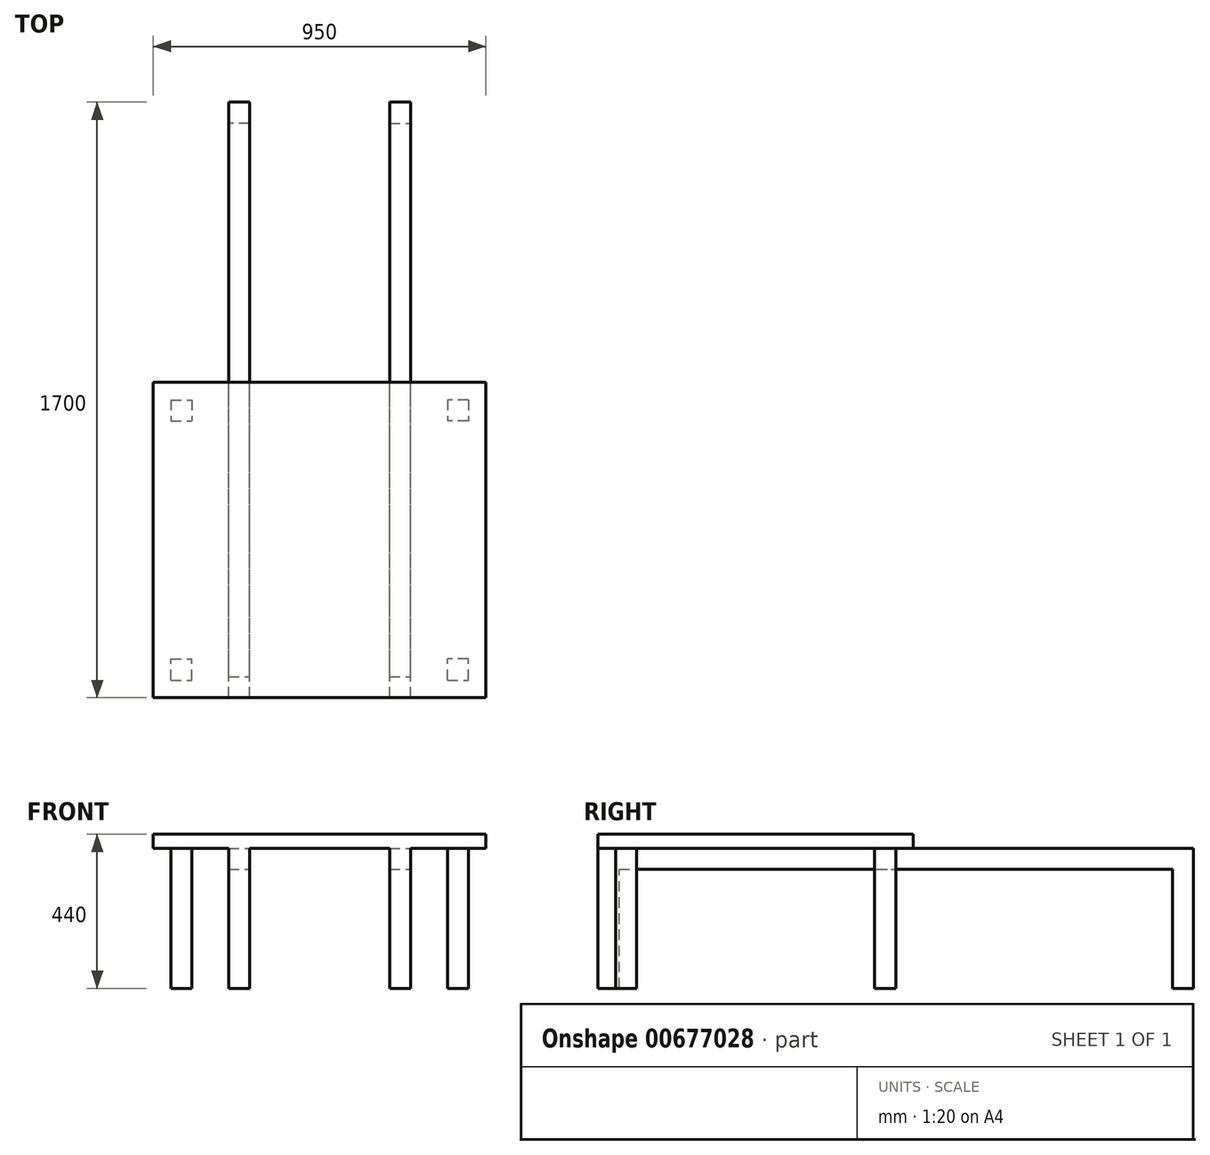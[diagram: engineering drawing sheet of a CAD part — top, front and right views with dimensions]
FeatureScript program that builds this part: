
annotation { "Feature Type Name" : "Feature", "Feature Type Description" : "" }
export const myFeature = defineFeature(function(context is Context, id is Id, definition is map)
    precondition{}
    {
        {
            var Q0;
            Q0=qCreatedBy(makeId("Top.planeOp"),FACE);
            var sketch = newSketch(context, id + "F0", { "sketchPlane" : qUnion([Q0])});
            skLineSegment(sketch, "E0", {"start": v(0, 1100) * mm, "end": v(0, 0) * mm, "construction": true});
            skLineSegment(sketch, "E1", {"start": v(-735, 500) * mm, "end": v(-735, 0) * mm, "construction": true});
            skLineSegment(sketch, "E2", {"start": v(-735, 0) * mm, "end": v(-485, 0) * mm, "construction": true});
            skLineSegment(sketch, "E3", {"start": v(-485, 0) * mm, "end": v(-735, 500) * mm, "construction": true});
            skLineSegment(sketch, "E4", {"start": v(735, 500) * mm, "end": v(485, 0) * mm, "construction": true});
            skLineSegment(sketch, "E5", {"start": v(-485, 496.22) * mm, "end": v(-485, 0) * mm});
            skLineSegment(sketch, "E6", {"start": v(485, 496.22) * mm, "end": v(485, 0) * mm});
            skLineSegment(sketch, "E7", {"start": v(-735, 500) * mm, "end": v(-735, 0) * mm});
            skLineSegment(sketch, "E8", {"start": v(-485, 0) * mm, "end": v(-485, 500) * mm});
            skLineSegment(sketch, "E9", {"start": v(-485, 500) * mm, "end": v(-735, 500) * mm});
            skLineSegment(sketch, "E10.MirrorCS", {"start": v(485, 500) * mm, "end": v(735, 500) * mm});
            skLineSegment(sketch, "E11.MirrorCS", {"start": v(485, 0) * mm, "end": v(485, 500) * mm});
            skLineSegment(sketch, "E12.MirrorCS", {"start": v(735, 0) * mm, "end": v(485, 0) * mm, "construction": true});
            skLineSegment(sketch, "E13.MirrorCS", {"start": v(735, 500) * mm, "end": v(735, 0) * mm, "construction": true});
            skLineSegment(sketch, "E14.top", {"start": v(-625, 1100) * mm, "end": v(625, 1100) * mm, "construction": true});
            skLineSegment(sketch, "E15", {"start": v(-475, 0) * mm, "end": v(-475, 900) * mm});
            skLineSegment(sketch, "E16", {"start": v(-475, 900) * mm, "end": v(475, 900) * mm});
            skLineSegment(sketch, "E17", {"start": v(475, 900) * mm, "end": v(475, 0) * mm});
            skLineSegment(sketch, "E18", {"start": v(-475, 0) * mm, "end": v(475, 0) * mm});
            skLineSegment(sketch, "E19.0", {"start": v(-425, 50) * mm, "end": v(-425, 850) * mm, "construction": true});
            skLineSegment(sketch, "E19.1", {"start": v(-425, 50) * mm, "end": v(425, 50) * mm, "construction": true});
            skLineSegment(sketch, "E19.2", {"start": v(425, 850) * mm, "end": v(425, 50) * mm, "construction": true});
            skLineSegment(sketch, "E19.3", {"start": v(-425, 850) * mm, "end": v(425, 850) * mm, "construction": true});
            skLineSegment(sketch, "E20.bottom", {"start": v(-425, 50) * mm, "end": v(-365, 50) * mm});
            skLineSegment(sketch, "E20.top", {"start": v(-425, 110) * mm, "end": v(-365, 110) * mm});
            skLineSegment(sketch, "E20.left", {"start": v(-425, 50) * mm, "end": v(-425, 110) * mm});
            skLineSegment(sketch, "E20.right", {"start": v(-365, 50) * mm, "end": v(-365, 110) * mm});
            skLineSegment(sketch, "E21.bottom", {"start": v(-425, 850) * mm, "end": v(-365, 850) * mm});
            skLineSegment(sketch, "E21.top", {"start": v(-425, 790) * mm, "end": v(-365, 790) * mm});
            skLineSegment(sketch, "E21.left", {"start": v(-425, 850) * mm, "end": v(-425, 790) * mm});
            skLineSegment(sketch, "E21.right", {"start": v(-365, 850) * mm, "end": v(-365, 790) * mm});
            skLineSegment(sketch, "E22.MirrorCS", {"start": v(365, 850) * mm, "end": v(365, 790) * mm});
            skLineSegment(sketch, "E23.MirrorCS", {"start": v(425, 850) * mm, "end": v(-425, 850) * mm, "construction": true});
            skLineSegment(sketch, "E24.MirrorCS", {"start": v(425, 50) * mm, "end": v(425, 850) * mm, "construction": true});
            skLineSegment(sketch, "E25.MirrorCS", {"start": v(425, 790) * mm, "end": v(365, 790) * mm});
            skLineSegment(sketch, "E26.MirrorCS", {"start": v(425, 110) * mm, "end": v(365, 110) * mm});
            skLineSegment(sketch, "E27.MirrorCS", {"start": v(365, 50) * mm, "end": v(365, 110) * mm});
            skLineSegment(sketch, "E28", {"start": v(425, 850) * mm, "end": v(425, 790) * mm});
            skLineSegment(sketch, "E29", {"start": v(365, 50) * mm, "end": v(425, 50) * mm});
            skLineSegment(sketch, "E30", {"start": v(425, 50) * mm, "end": v(425, 110) * mm});
            skLineSegment(sketch, "E31", {"start": v(-425, 110) * mm, "end": v(-425, 50) * mm});
            skLineSegment(sketch, "E32", {"start": v(425, 850) * mm, "end": v(365, 850) * mm});
            skSolve(sketch);
        }
        {
            var Q0;
            Q0=makeQuery(id+"F0.imprint","IMPRINT",FACE,{"disambiguationData":[TD([[makeQuery(id+"F0.imprint","IMPRINT",EDGE,{"derivedFrom":sQuery(id+"F0.wireOp",EDGE,"E15")}),-1.0]])]});
            var Q1;
            Q1=makeQuery(id+"F0.imprint","IMPRINT",FACE,{"disambiguationData":[TD([[makeQuery(id+"F0.imprint","IMPRINT",EDGE,{"derivedFrom":sQuery(id+"F0.wireOp",EDGE,"1b7d4963-c026-4f4c-91ac-6df9d517a1e60.MirrorCS")}),-1.0]])]});
            var Q2;
            Q2=makeQuery(id+"F0.imprint","IMPRINT",FACE,{"disambiguationData":[TD([[makeQuery(id+"F0.imprint","IMPRINT",EDGE,{"derivedFrom":sQuery(id+"F0.wireOp",EDGE,"E20.bottom")}),1.0]])]});
            var Q3;
            Q3=makeQuery(id+"F0.imprint","IMPRINT",FACE,{"disambiguationData":[TD([[makeQuery(id+"F0.imprint","IMPRINT",EDGE,{"derivedFrom":sQuery(id+"F0.wireOp",EDGE,"E21.bottom")}),-1.0]])]});
            var Q4;
            Q4=makeQuery(id+"F0.imprint","IMPRINT",FACE,{"disambiguationData":[TD([[makeQuery(id+"F0.imprint","IMPRINT",EDGE,{"derivedFrom":sQuery(id+"F0.wireOp",EDGE,"37fc98a1-9a7f-4c86-b700-b2ec89ce71ce0.MirrorCS")}),1.0]])]});
            var Q5;
            Q5=makeQuery(id+"F0.imprint","IMPRINT",FACE,{"disambiguationData":[TD([[makeQuery(id+"F0.imprint","IMPRINT",EDGE,{"derivedFrom":sQuery(id+"F0.wireOp",EDGE,"E26.MirrorCS")}),1.0]])]});
            var Q6;
            Q6=makeQuery(id+"F0.imprint","IMPRINT",FACE,{"disambiguationData":[TD([[makeQuery(id+"F0.imprint","IMPRINT",EDGE,{"derivedFrom":sQuery(id+"F0.wireOp",EDGE,"E22.MirrorCS")}),1.0]])]});
            extrude(context, id + "F1", {"entities" : qUnion([Q0, Q1, Q2, Q3, Q4, Q5, Q6]), "depth" : 40 * mm, "offsetDistance" : 25 * mm});
        }
        {
            var Q0;
            Q0=makeQuery(id+"F0.imprint","IMPRINT",FACE,{"disambiguationData":[TD([[makeQuery(id+"F0.imprint","IMPRINT",EDGE,{"derivedFrom":sQuery(id+"F0.wireOp",EDGE,"37fc98a1-9a7f-4c86-b700-b2ec89ce71ce0.MirrorCS")}),1.0]])]});
            var Q1;
            Q1=makeQuery(id+"F0.imprint","IMPRINT",FACE,{"disambiguationData":[TD([[makeQuery(id+"F0.imprint","IMPRINT",EDGE,{"derivedFrom":sQuery(id+"F0.wireOp",EDGE,"E20.bottom")}),1.0]])]});
            var Q2;
            Q2=makeQuery(id+"F0.imprint","IMPRINT",FACE,{"disambiguationData":[TD([[makeQuery(id+"F0.imprint","IMPRINT",EDGE,{"derivedFrom":sQuery(id+"F0.wireOp",EDGE,"E21.bottom")}),-1.0]])]});
            var Q3;
            Q3=makeQuery(id+"F0.imprint","IMPRINT",FACE,{"disambiguationData":[TD([[makeQuery(id+"F0.imprint","IMPRINT",EDGE,{"derivedFrom":sQuery(id+"F0.wireOp",EDGE,"1b7d4963-c026-4f4c-91ac-6df9d517a1e60.MirrorCS")}),-1.0]])]});
            var Q4;
            Q4=makeQuery(id+"F0.imprint","IMPRINT",FACE,{"disambiguationData":[TD([[makeQuery(id+"F0.imprint","IMPRINT",EDGE,{"derivedFrom":sQuery(id+"F0.wireOp",EDGE,"E26.MirrorCS")}),1.0]])]});
            var Q5;
            Q5=makeQuery(id+"F0.imprint","IMPRINT",FACE,{"disambiguationData":[TD([[makeQuery(id+"F0.imprint","IMPRINT",EDGE,{"derivedFrom":sQuery(id+"F0.wireOp",EDGE,"E22.MirrorCS")}),1.0]])]});
            extrude(context, id + "F2", {"entities" : qUnion([Q0, Q1, Q2, Q3, Q4, Q5]), "operationType" : NewBodyOperationType.ADD, "oppositeDirection" : true, "depth" : 400 * mm, "offsetDistance" : 25 * mm});
        }
        {
            var Q0;
            Q0=makeQuery(id+"F1.opExtrude","CAP_FACE",FACE,{"disambiguationData":[OSD([sQuery(id+"F0.wireOp",EDGE,"E15"),sQuery(id+"F0.wireOp",EDGE,"E16"),sQuery(id+"F0.wireOp",EDGE,"E17"),sQuery(id+"F0.wireOp",EDGE,"E18")])],"isStart":true});
            var sketch = newSketch(context, id + "F3", { "sketchPlane" : qUnion([Q0])});
            skLineSegment(sketch, "E33", {"start": v(0, 0) * mm, "end": v(0, -900) * mm, "construction": true});
            skLineSegment(sketch, "E34.bottom", {"start": v(-260, 0) * mm, "end": v(-200, 0) * mm});
            skLineSegment(sketch, "E34.top", {"start": v(-260, -1700) * mm, "end": v(-200, -1700) * mm});
            skLineSegment(sketch, "E34.left", {"start": v(-260, 0) * mm, "end": v(-260, -1700) * mm});
            skLineSegment(sketch, "E34.right", {"start": v(-200, 0) * mm, "end": v(-200, -1700) * mm});
            skLineSegment(sketch, "E35.MirrorCS", {"start": v(200, 0) * mm, "end": v(200, -1700) * mm});
            skLineSegment(sketch, "E36.MirrorCS", {"start": v(260, 0) * mm, "end": v(260, -1700) * mm});
            skLineSegment(sketch, "E37.MirrorCS", {"start": v(260, 0) * mm, "end": v(200, 0) * mm});
            skLineSegment(sketch, "E38.MirrorCS", {"start": v(260, -1700) * mm, "end": v(200, -1700) * mm});
            skSolve(sketch);
        }
        {
            var Q0;
            Q0 = qSketchRegion(id + "F3", true);
            extrude(context, id + "F4", {"entities" : qUnion([Q0]), "operationType" : NewBodyOperationType.ADD, "depth" : 60 * mm, "offsetDistance" : 25 * mm});
        }
        {
            var Q0;
            Q0 = qSketchRegion(id + "F3", true);
            extrude(context, id + "F5", {"entities" : qUnion([Q0]), "operationType" : NewBodyOperationType.ADD, "depth" : 60 * mm, "offsetDistance" : 25 * mm});
        }
        {
            var Q0;
            Q0=makeQuery(id+"F4.opExtrude","CAP_FACE",FACE,{"disambiguationData":[OSD([sQuery(id+"F3.wireOp",EDGE,"E35.MirrorCS"),sQuery(id+"F3.wireOp",EDGE,"E36.MirrorCS"),sQuery(id+"F3.wireOp",EDGE,"E37.MirrorCS"),sQuery(id+"F3.wireOp",EDGE,"E38.MirrorCS")])],"isStart":false});
            var sketch = newSketch(context, id + "F6", { "sketchPlane" : qUnion([Q0])});
            skLineSegment(sketch, "E39.bottom", {"start": v(-200, -1700) * mm, "end": v(-260, -1700) * mm});
            skLineSegment(sketch, "E39.top", {"start": v(-200, -1640) * mm, "end": v(-260, -1640) * mm});
            skLineSegment(sketch, "E39.left", {"start": v(-200, -1700) * mm, "end": v(-200, -1640) * mm});
            skLineSegment(sketch, "E39.right", {"start": v(-260, -1700) * mm, "end": v(-260, -1640) * mm});
            skLineSegment(sketch, "E40.MirrorCS", {"start": v(200, -1700) * mm, "end": v(200, -1640) * mm});
            skLineSegment(sketch, "E41.MirrorCS", {"start": v(260, -1700) * mm, "end": v(260, -1640) * mm});
            skLineSegment(sketch, "E42.MirrorCS", {"start": v(200, -1700) * mm, "end": v(260, -1700) * mm});
            skLineSegment(sketch, "E43.MirrorCS", {"start": v(200, -1640) * mm, "end": v(260, -1640) * mm});
            skLineSegment(sketch, "E44.bottom", {"start": v(-260, 0) * mm, "end": v(-200, 0) * mm});
            skLineSegment(sketch, "E44.top", {"start": v(-260, -60) * mm, "end": v(-200, -60) * mm});
            skLineSegment(sketch, "E44.left", {"start": v(-260, 0) * mm, "end": v(-260, -60) * mm});
            skLineSegment(sketch, "E44.right", {"start": v(-200, 0) * mm, "end": v(-200, -60) * mm});
            skLineSegment(sketch, "E45.bottom", {"start": v(200, 0) * mm, "end": v(260, 0) * mm});
            skLineSegment(sketch, "E45.top", {"start": v(200, -60) * mm, "end": v(260, -60) * mm});
            skLineSegment(sketch, "E45.left", {"start": v(200, 0) * mm, "end": v(200, -60) * mm});
            skLineSegment(sketch, "E45.right", {"start": v(260, 0) * mm, "end": v(260, -60) * mm});
            skSolve(sketch);
        }
        {
            var Q0;
            Q0=makeQuery(id+"F6.imprint","IMPRINT",FACE,{"disambiguationData":[TD([[makeQuery(id+"F6.imprint","IMPRINT",EDGE,{"derivedFrom":sQuery(id+"F6.wireOp",EDGE,"E40.MirrorCS")}),1.0]])]});
            var Q1;
            Q1=makeQuery(id+"F6.imprint","IMPRINT",FACE,{"disambiguationData":[TD([[makeQuery(id+"F6.imprint","IMPRINT",EDGE,{"derivedFrom":sQuery(id+"F6.wireOp",EDGE,"E39.bottom")}),-1.0]])]});
            var Q2;
            Q2=makeQuery(id+"F6.imprint","IMPRINT",FACE,{"disambiguationData":[TD([[makeQuery(id+"F6.imprint","IMPRINT",EDGE,{"derivedFrom":sQuery(id+"F6.wireOp",EDGE,"E44.bottom")}),-1.0]])]});
            var Q3;
            Q3=makeQuery(id+"F6.imprint","IMPRINT",FACE,{"disambiguationData":[TD([[makeQuery(id+"F6.imprint","IMPRINT",EDGE,{"derivedFrom":sQuery(id+"F6.wireOp",EDGE,"E45.bottom")}),-1.0]])]});
            extrude(context, id + "F7", {"entities" : qUnion([Q0, Q1, Q2, Q3]), "operationType" : NewBodyOperationType.ADD, "depth" : 340 * mm, "offsetDistance" : 25 * mm});
        }
    });
